# Revit family: QF_ELECTROLUXPROFESSIONAL_1LSN95_WH6-20_S
name_source: partatom
category: Attrezzature speciali
units: mm (PartAtom-declared; Revit-internal decimal feet)

## family parameters
Basato su piano di lavoro = No
Condiviso = No
Punto di calcolo locali = No
Quota connettore circolare = Usa diametro
Sempre verticale = Sì
Taglio con vuoti quando caricato = No
Tipo di parte = Normale

## types (10) — shared parameters
Depth Actual = 947 mm  [stored 3.10696 ft]
Height Actual = 1412 mm  [stored 4.63255 ft]
Latent Heat Output = 0.0
Length Actual = 970 mm  [stored 3.18241 ft]
Modello = WH6-20
Produttore = Electrolux Professional
Sensible Heat Output = 0.0
URL = www.electroluxprofessional.com
Watts = 2500 W
Weight = 354
zero-valued in all types: Gas KW, Prospetto di default, Steam Pounds per Hour

## per-type parameters (varying)
| type | Cycle | Descrizione | Item Number | Phase | Volts |
| 9867930255 | 50 Hz | WASHER WH6-20 20KG STEAM 220-240/50/1N COMPASS PRO 6H01 ML 2xWATER POWDER+5xLIQ. EL.VALV.OPEN SILVER 2.I/O DISCON. STOP | 1L0HDS | 1 | 240 V |
| 9867930133 | 50 Hz | WASHER WH6-20 20KG STEAM 220-240/50/1N COMPASS PRO 6G01 CH-EN 2xWATER POWDER+5xLIQ. VALV.OPEN SILVER 2.I/O DISCON. STOP | 1L0GCD | 1 | 240 V |
| 9867930194 | 50 Hz | WASHER WH6-20 20KG STEAM 200/50/60/3 COMPASS PRO 6H43 JP,EN 2xWATER POWDER+5xLIQ. VALV.OPEN SILVER 2.I/O DISCON. | 1L0GRK | 3 | 200 V |
| 9867930153 | 50 Hz | WASHER WH6-20 20KG STEAM 220-240/50/1N COMPASS PRO 6G01 ML 2xWATER POWDER+5xLIQ. VALV.OPEN SILVER 2.I/O DISCON. STOP | 1L8264 | 1 | 240 V |
| 9867930270 | 50 Hz | WASHER WH6-20 20KG STEAM 220-240/50/1N COMPASS PRO 6L01 ML 2xWATER POWDER EL.VALV.OPEN SST DISCON. | 1L0HER | 1 | 240 V |
| 9867930177 | 50 Hz | WASHER WH6-20 20KG STEAM 220-240/50/1N COMPASS PRO 6H12 ML 2xWATER POWDER+5xLIQ. EL.VALV.CLOSED SILVER 2.I/O DISCON. STO | 1L0GKA | 1 | 240 V |
| 9867930142 | 50 Hz | WASHER WH6-20 20KG STEAM 200/50/60/3 COMPASS PRO 6H43 JP,EN 2xWATER POWDER+5xLIQ. VALV.OPEN SST 2.I/O DISCON. | 1LA1AM | 3 | 200 V |
| 9867930089 | 50 Hz | WASHER WH6-20 20KG STEAM 220-240/50/1N COMPASS PRO 6G01 ML 2xWATER POWDER+5xLIQ. VALV.OPEN SST/SILVER 2.I/O QC DISCON. S | 1LSP5X | 1 | 240 V |
| 9867930176 | 60 Hz | WASHER WH6-20 20KG STEAM 220-240/60/1N COMPASS PRO 6G07 ML 2xWATER POWDER+5xLIQ. VALV.OPEN SILVER 2.I/O DISCON. STOP | 1L0GK9 | 1 | 240 V |
| 9867930118 | 50 Hz | WASHER WH6-20 20KG STEAM 220-240/50/1N COMPASS PRO 6G01 ML 2xWATER POWDER+5xLIQ. VALV.OPEN SILVER 2.I/O QC DISCON. STOP | 1L8221 | 1 | 240 V |

note: [stored X ft] marks values corroborated as IEEE doubles in the binary element streams (Revit-internal decimal feet)

## geometry (parser evidence)
native form markers: Blend x4
no freeform markers — native parametric forms only
